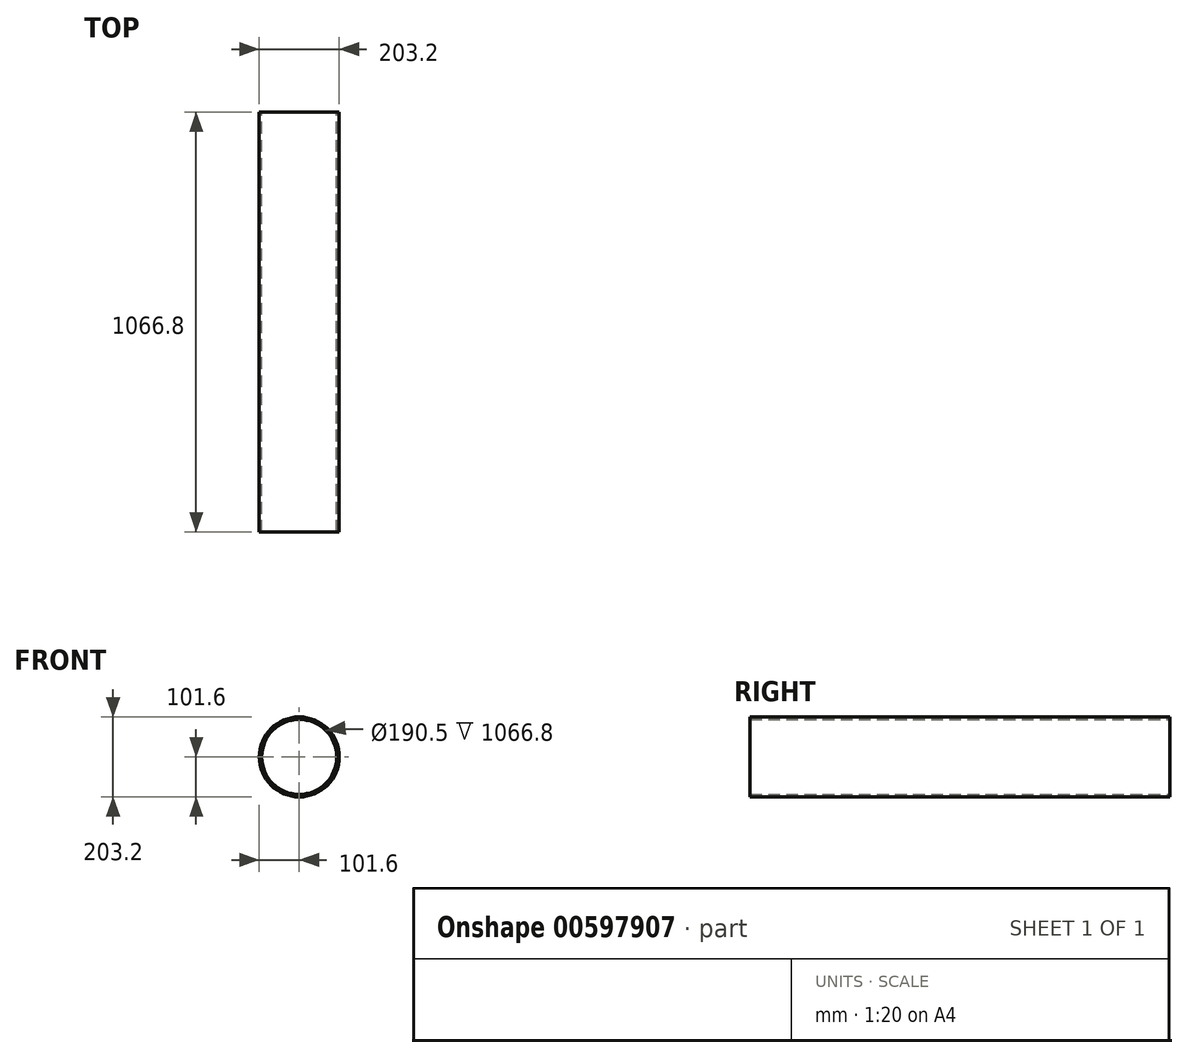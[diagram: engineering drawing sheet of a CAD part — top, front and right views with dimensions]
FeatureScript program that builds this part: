
annotation { "Feature Type Name" : "Feature", "Feature Type Description" : "" }
export const myFeature = defineFeature(function(context is Context, id is Id, definition is map)
    precondition{}
    {
        {
            var Q0;
            Q0=qCreatedBy(makeId("Front.planeOp"),FACE);
            var sketch = newSketch(context, id + "F0", { "sketchPlane" : qUnion([Q0])});
            skCircle(sketch, "E0", {"center": v(0, 0) * mm, "radius": 101.6 * mm});
            skCircle(sketch, "E1", {"center": v(0, 0) * mm, "radius": 95.25 * mm});
            skSolve(sketch);
        }
        {
            var Q0;
            Q0 = qSketchRegion(id + "F0", true);
            extrude(context, id + "F1", {"entities" : qUnion([Q0]), "depth" : 1066.8 * mm, "offsetDistance" : 25.4 * mm});
        }
    });
